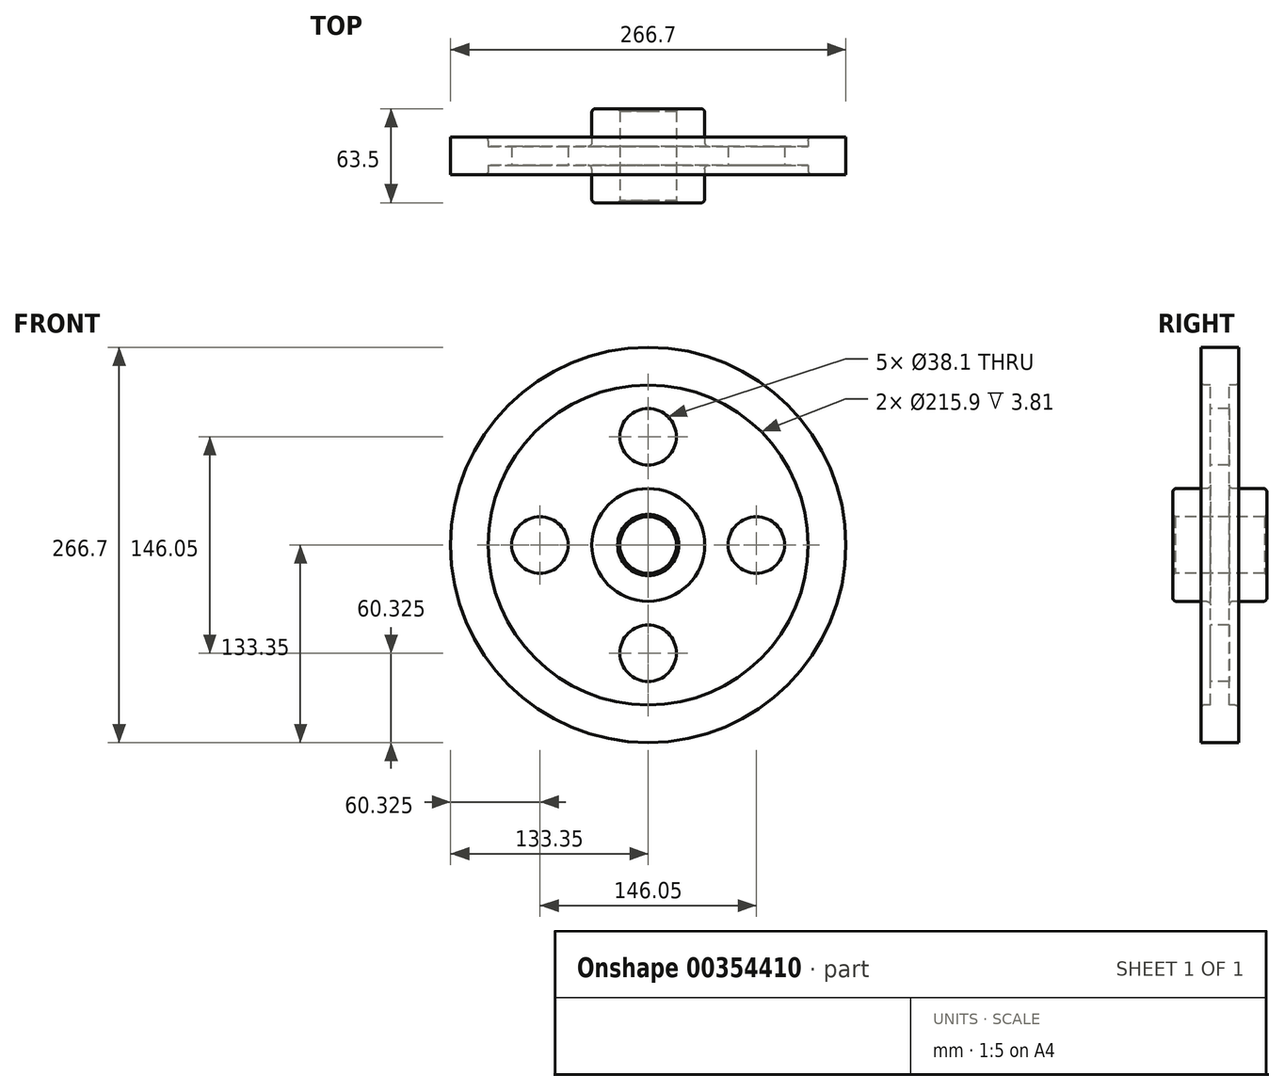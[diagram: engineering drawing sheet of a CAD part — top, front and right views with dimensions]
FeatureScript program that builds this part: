
annotation { "Feature Type Name" : "Feature", "Feature Type Description" : "" }
export const myFeature = defineFeature(function(context is Context, id is Id, definition is map)
    precondition{}
    {
        {
            var Q0;
            Q0=qCreatedBy(makeId("Right.planeOp"),FACE);
            var sketch = newSketch(context, id + "F0", { "sketchPlane" : qUnion([Q0])});
            skLineSegment(sketch, "E0", {"start": v(0, 0) * mm, "end": v(31.75, 0) * mm, "construction": true});
            skLineSegment(sketch, "E1.0", {"start": v(0, 19.05) * mm, "end": v(31.75, 19.05) * mm});
            skLineSegment(sketch, "E2.0", {"start": v(6.35, 38.1) * mm, "end": v(31.75, 38.1) * mm});
            skLineSegment(sketch, "E3.0", {"start": v(6.35, 107.95) * mm, "end": v(12.7, 107.95) * mm});
            skLineSegment(sketch, "E4.0", {"start": v(0, 133.35) * mm, "end": v(12.7, 133.35) * mm});
            skLineSegment(sketch, "E5", {"start": v(0, 133.35) * mm, "end": v(0, 0) * mm});
            skLineSegment(sketch, "E6.0", {"start": v(31.75, 38.1) * mm, "end": v(31.75, 19.05) * mm});
            skLineSegment(sketch, "E7.0", {"start": v(6.35, 107.95) * mm, "end": v(6.35, 38.1) * mm});
            skLineSegment(sketch, "E8.0", {"start": v(12.7, 133.35) * mm, "end": v(12.7, 107.95) * mm});
            skLineSegment(sketch, "E9.MirrorCS", {"start": v(0, 133.35) * mm, "end": v(-12.7, 133.35) * mm});
            skLineSegment(sketch, "E10.MirrorCS", {"start": v(-12.7, 133.35) * mm, "end": v(-12.7, 107.95) * mm});
            skLineSegment(sketch, "E11.MirrorCS", {"start": v(-6.35, 107.95) * mm, "end": v(-6.35, 38.1) * mm});
            skLineSegment(sketch, "E12.MirrorCS", {"start": v(-6.35, 38.1) * mm, "end": v(-31.75, 38.1) * mm});
            skLineSegment(sketch, "E13.MirrorCS", {"start": v(-31.75, 38.1) * mm, "end": v(-31.75, 19.05) * mm});
            skLineSegment(sketch, "E14.MirrorCS", {"start": v(0, 19.05) * mm, "end": v(-31.75, 19.05) * mm});
            skLineSegment(sketch, "E15", {"start": v(-12.7, 107.95) * mm, "end": v(-6.35, 107.95) * mm});
            skSolve(sketch);
        }
        {
            var Q0;
            {var subQ1=sQuery(id+"F0.wireOp",EDGE,"E1.0");Q0=makeQuery(id+"F0.imprint","IMPRINT",FACE,{"disambiguationData":[TD([[makeQuery(id+"F0.imprint","IMPRINT",EDGE,{"derivedFrom":subQ1}),1.0]])]});}
            var Q1;
            {var subQ0=sQuery(id+"F0.wireOp",EDGE,"E9.MirrorCS");Q1=makeQuery(id+"F0.imprint","IMPRINT",FACE,{"disambiguationData":[TD([[makeQuery(id+"F0.imprint","IMPRINT",EDGE,{"derivedFrom":subQ0}),1.0]])]});}
            var Q2;
            Q2=sQuery(id+"F0.wireOp",EDGE,"E0");
            revolve(context, id + "F1", {"entities" : qUnion([Q0, Q1]), "axis" : qUnion([Q2]), "revolveType" : RevolveType.FULL});
        }
        {
            var Q0;
            Q0=makeQuery(id+"F1.opRevolve","SWEPT_FACE",FACE,{"disambiguationData":[OSD([sQuery(id+"F0.wireOp",EDGE,"E11.MirrorCS")])]});
            var sketch = newSketch(context, id + "F2", { "sketchPlane" : qUnion([Q0])});
            skLineSegment(sketch, "E16", {"start": v(0, 0) * mm, "end": v(0, 73.03) * mm});
            skCircle(sketch, "E17", {"center": v(0, 73.03) * mm, "radius": 19.05 * mm});
            skCircle(sketch, "E18.1.0", {"center": v(-73.03, 0) * mm, "radius": 19.05 * mm});
            skCircle(sketch, "E18.2.0", {"center": v(0, -73.03) * mm, "radius": 19.05 * mm});
            skPoint(sketch, "E18.center", {"position": v(0, 0) * mm});
            skCircle(sketch, "E19.1.3.0", {"center": v(73.03, 0) * mm, "radius": 19.05 * mm});
            skSolve(sketch);
        }
        {
            var Q0;
            Q0=makeQuery(id+"F2.imprint","IMPRINT",FACE,{"disambiguationData":[TD([[makeQuery(id+"F2.imprint","IMPRINT",EDGE,{"derivedFrom":sQuery(id+"F2.wireOp",EDGE,"E19.1.3.0")}),1.0]])]});
            var Q1;
            Q1=makeQuery(id+"F2.imprint","IMPRINT",FACE,{"disambiguationData":[TD([[makeQuery(id+"F2.imprint","IMPRINT",EDGE,{"derivedFrom":sQuery(id+"F2.wireOp",EDGE,"E17")}),1.0]])]});
            var Q2;
            Q2=makeQuery(id+"F2.imprint","IMPRINT",FACE,{"disambiguationData":[TD([[makeQuery(id+"F2.imprint","IMPRINT",EDGE,{"derivedFrom":sQuery(id+"F2.wireOp",EDGE,"E18.1.0")}),1.0]])]});
            var Q3;
            Q3=makeQuery(id+"F2.imprint","IMPRINT",FACE,{"disambiguationData":[TD([[makeQuery(id+"F2.imprint","IMPRINT",EDGE,{"derivedFrom":sQuery(id+"F2.wireOp",EDGE,"E18.2.0")}),1.0]])]});
            extrude(context, id + "F3", {"entities" : qUnion([Q0, Q1, Q2, Q3]), "operationType" : NewBodyOperationType.REMOVE, "oppositeDirection" : true, "depth" : 25.4 * mm});
        }
        {
            var Q0;
            Q0=makeQuery(id+"F1.opRevolve","SWEPT_EDGE",EDGE,{"disambiguationData":[OSD([sQuery(id+"F0.wireOp",EDGE,"E10.MirrorCS"),sQuery(id+"F0.wireOp",EDGE,"E15")])]});
            var Q1;
            Q1=makeQuery(id+"F1.opRevolve","SWEPT_EDGE",EDGE,{"disambiguationData":[OSD([sQuery(id+"F0.wireOp",EDGE,"E3.0"),sQuery(id+"F0.wireOp",EDGE,"E8.0")])]});
            var Q2;
            Q2=makeQuery(id+"F1.opRevolve","SWEPT_EDGE",EDGE,{"disambiguationData":[OSD([sQuery(id+"F0.wireOp",EDGE,"E2.0"),sQuery(id+"F0.wireOp",EDGE,"E7.0")])]});
            var Q3;
            Q3=makeQuery(id+"F1.opRevolve","SWEPT_EDGE",EDGE,{"disambiguationData":[OSD([sQuery(id+"F0.wireOp",EDGE,"E11.MirrorCS"),sQuery(id+"F0.wireOp",EDGE,"E12.MirrorCS")])]});
            var Q4;
            Q4=makeQuery(id+"F1.opRevolve","SWEPT_EDGE",EDGE,{"disambiguationData":[OSD([sQuery(id+"F0.wireOp",EDGE,"E12.MirrorCS"),sQuery(id+"F0.wireOp",EDGE,"E13.MirrorCS")])]});
            var Q5;
            Q5=makeQuery(id+"F1.opRevolve","SWEPT_EDGE",EDGE,{"disambiguationData":[OSD([sQuery(id+"F0.wireOp",EDGE,"E2.0"),sQuery(id+"F0.wireOp",EDGE,"E6.0")])]});
            fillet(context, id + "F4", {"entities" : qUnion([Q0, Q1, Q2, Q3, Q4, Q5]), "radius" : 2.54 * mm, "tangentPropagation" : true, "allowEdgeOverflow" : false});
        }
        {
            var Q0;
            Q0=makeQuery(id+"F1.opRevolve","SWEPT_EDGE",EDGE,{"disambiguationData":[OSD([sQuery(id+"F0.wireOp",EDGE,"E13.MirrorCS"),sQuery(id+"F0.wireOp",EDGE,"E14.MirrorCS")])]});
            var Q1;
            Q1=makeQuery(id+"F1.opRevolve","SWEPT_EDGE",EDGE,{"disambiguationData":[OSD([sQuery(id+"F0.wireOp",EDGE,"E1.0"),sQuery(id+"F0.wireOp",EDGE,"E6.0")])]});
            chamfer(context, id + "F5", {"entities" : qUnion([Q0, Q1]), "width" : 1.59 * mm, "tangentPropagation" : true});
        }
    });
